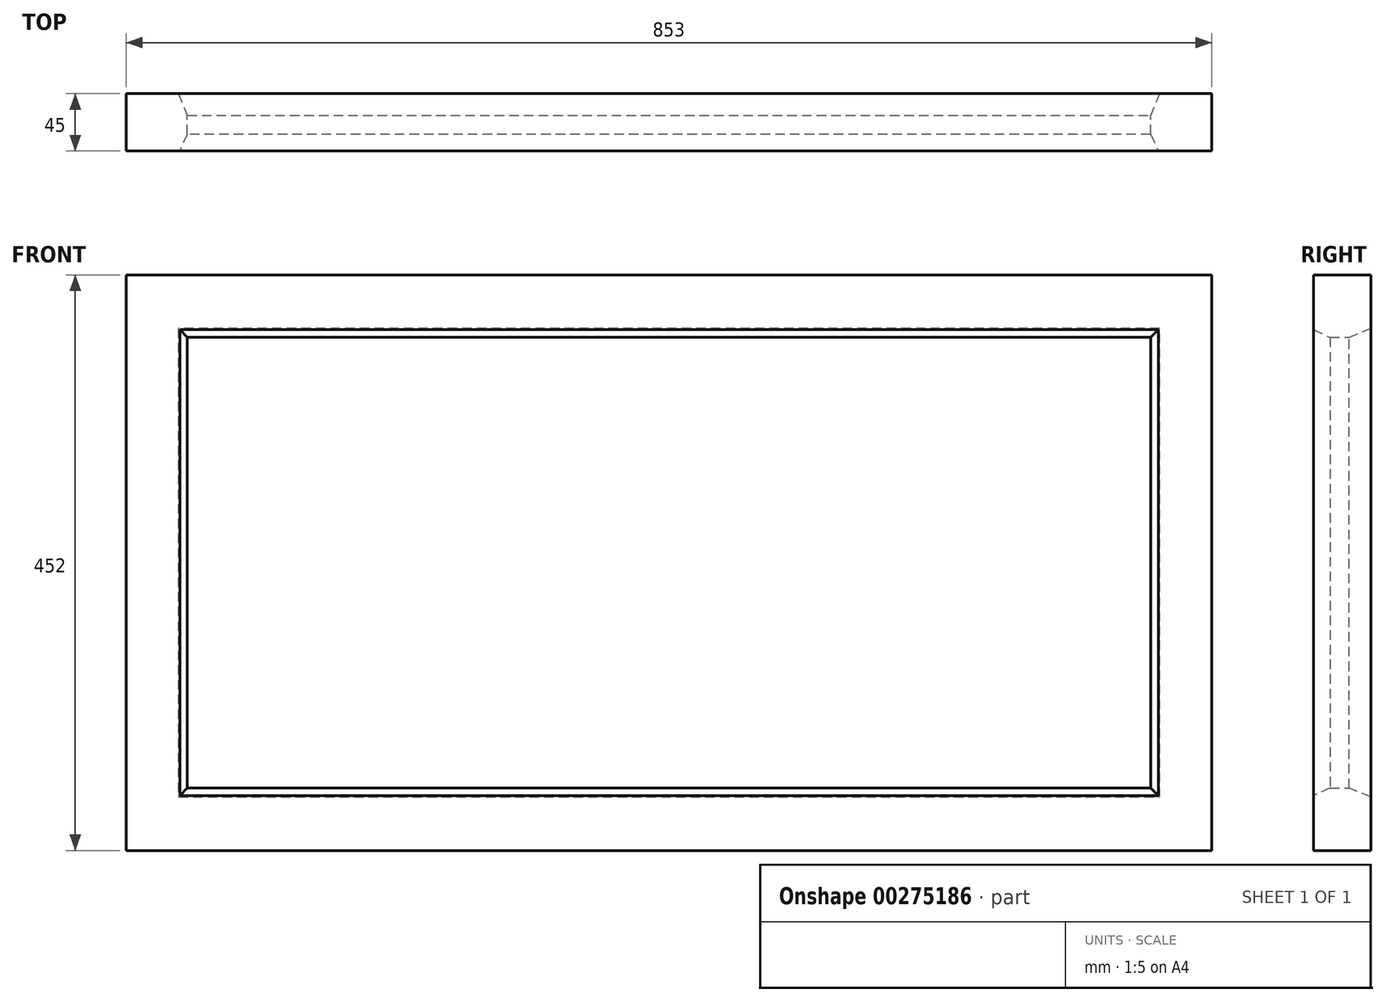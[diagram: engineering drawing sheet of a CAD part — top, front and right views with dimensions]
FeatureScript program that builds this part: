
annotation { "Feature Type Name" : "Feature", "Feature Type Description" : "" }
export const myFeature = defineFeature(function(context is Context, id is Id, definition is map)
    precondition{}
    {
        {
            var Q0;
            Q0=qCreatedBy(makeId("Front.planeOp"),FACE);
            var sketch = newSketch(context, id + "F0", { "sketchPlane" : qUnion([Q0])});
            skLineSegment(sketch, "E0.bottom", {"start": v(-426.5, 226) * mm, "end": v(426.5, 226) * mm});
            skLineSegment(sketch, "E0.top", {"start": v(-426.5, -226) * mm, "end": v(426.5, -226) * mm});
            skLineSegment(sketch, "E0.left", {"start": v(-426.5, 226) * mm, "end": v(-426.5, -226) * mm});
            skLineSegment(sketch, "E0.right", {"start": v(426.5, 226) * mm, "end": v(426.5, -226) * mm});
            skPoint(sketch, "E0.middle", {"position": v(0, 0) * mm});
            skLineSegment(sketch, "E1.bottom", {"start": v(-378.5, 177) * mm, "end": v(378.5, 177) * mm});
            skLineSegment(sketch, "E1.top", {"start": v(-378.5, -177) * mm, "end": v(378.5, -177) * mm});
            skLineSegment(sketch, "E1.left", {"start": v(-378.5, 177) * mm, "end": v(-378.5, -177) * mm});
            skLineSegment(sketch, "E1.right", {"start": v(378.5, 177) * mm, "end": v(378.5, -177) * mm});
            skSolve(sketch);
        }
        {
            var Q0;
            Q0 = qSketchRegion(id + "F0", true);
            extrude(context, id + "F1", {"entities" : qUnion([Q0]), "endBound" : BoundingType.SYMMETRIC, "depth" : 45 * mm});
        }
        {
            var Q0;
            Q0=makeQuery(id+"F1.opExtrude","CAP_EDGE",EDGE,{"disambiguationData":[OSD([sQuery(id+"F0.wireOp",EDGE,"E1.top")])],"isStart":false});
            var Q1;
            Q1=makeQuery(id+"F1.opExtrude","CAP_EDGE",EDGE,{"disambiguationData":[OSD([sQuery(id+"F0.wireOp",EDGE,"E1.left")])],"isStart":false});
            var Q2;
            Q2=makeQuery(id+"F1.opExtrude","CAP_EDGE",EDGE,{"disambiguationData":[OSD([sQuery(id+"F0.wireOp",EDGE,"E1.right")])],"isStart":false});
            var Q3;
            Q3=makeQuery(id+"F1.opExtrude","CAP_EDGE",EDGE,{"disambiguationData":[OSD([sQuery(id+"F0.wireOp",EDGE,"E1.bottom")])],"isStart":false});
            chamfer(context, id + "F2", {"entities" : qUnion([Q0, Q1, Q2, Q3]), "chamferType" : ChamferType.TWO_OFFSETS, "width1" : 6 * mm, "oppositeDirection" : true, "width2" : 13 * mm, "tangentPropagation" : true});
        }
        {
            var Q0;
            Q0=makeQuery(id+"F1.opExtrude","CAP_EDGE",EDGE,{"disambiguationData":[OSD([sQuery(id+"F0.wireOp",EDGE,"E1.top")])],"isStart":true});
            var Q1;
            Q1=makeQuery(id+"F1.opExtrude","CAP_EDGE",EDGE,{"disambiguationData":[OSD([sQuery(id+"F0.wireOp",EDGE,"E1.left")])],"isStart":true});
            var Q2;
            Q2=makeQuery(id+"F1.opExtrude","CAP_EDGE",EDGE,{"disambiguationData":[OSD([sQuery(id+"F0.wireOp",EDGE,"E1.bottom")])],"isStart":true});
            var Q3;
            Q3=makeQuery(id+"F1.opExtrude","CAP_EDGE",EDGE,{"disambiguationData":[OSD([sQuery(id+"F0.wireOp",EDGE,"E1.right")])],"isStart":true});
            chamfer(context, id + "F3", {"entities" : qUnion([Q0, Q1, Q2, Q3]), "chamferType" : ChamferType.TWO_OFFSETS, "width1" : 17 * mm, "oppositeDirection" : true, "width2" : 7 * mm, "tangentPropagation" : true});
        }
    });
